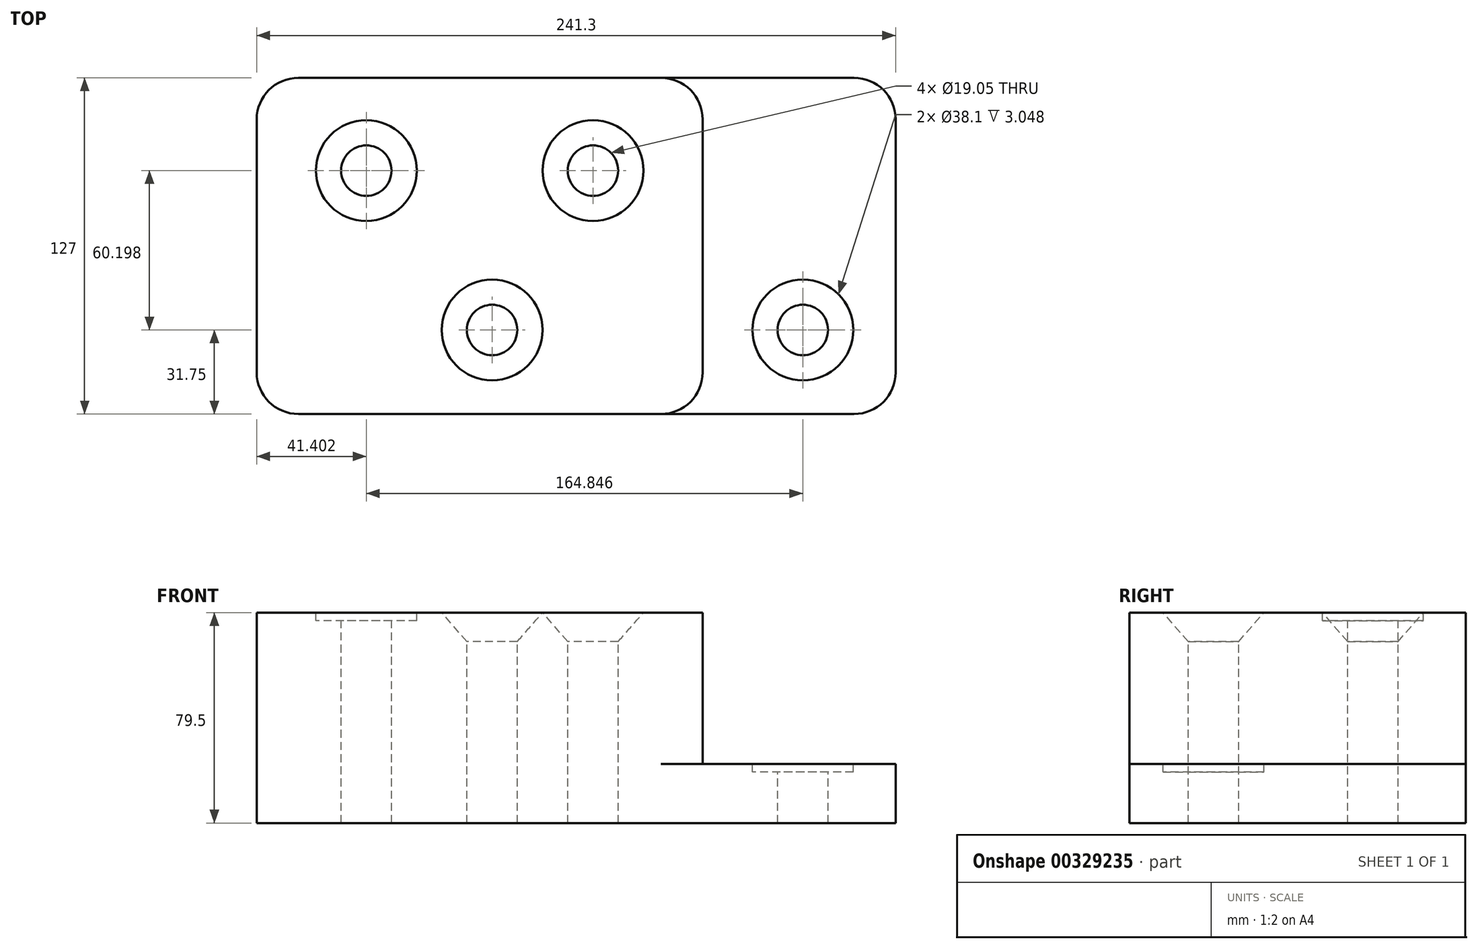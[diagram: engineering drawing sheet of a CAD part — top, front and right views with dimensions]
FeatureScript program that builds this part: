
annotation { "Feature Type Name" : "Feature", "Feature Type Description" : "" }
export const myFeature = defineFeature(function(context is Context, id is Id, definition is map)
    precondition{}
    {
        {
            var Q0;
            Q0=qCreatedBy(makeId("Front.planeOp"),FACE);
            var sketch = newSketch(context, id + "F0", { "sketchPlane" : qUnion([Q0])});
            skLineSegment(sketch, "E0", {"start": v(0, 0) * mm, "end": v(0, 79.5) * mm});
            skLineSegment(sketch, "E1", {"start": v(0, 79.5) * mm, "end": v(168.4, 79.5) * mm});
            skLineSegment(sketch, "E2", {"start": v(168.4, 79.5) * mm, "end": v(168.4, 22.35) * mm});
            skLineSegment(sketch, "E3", {"start": v(168.4, 22.35) * mm, "end": v(241.3, 22.35) * mm});
            skLineSegment(sketch, "E4", {"start": v(241.3, 22.35) * mm, "end": v(241.3, 0) * mm});
            skLineSegment(sketch, "E5", {"start": v(241.3, 0) * mm, "end": v(0, 0) * mm});
            skSolve(sketch);
        }
        {
            var Q0;
            Q0 = qSketchRegion(id + "F0", true);
            extrude(context, id + "F1", {"entities" : qUnion([Q0]), "depth" : 127 * mm});
        }
        {
            var Q0;
            Q0=makeQuery(id+"F1.opExtrude","CAP_EDGE",EDGE,{"disambiguationData":[OSD([sQuery(id+"F0.wireOp",EDGE,"E4")])],"isStart":false});
            var Q1;
            Q1=makeQuery(id+"F1.opExtrude","CAP_EDGE",EDGE,{"disambiguationData":[OSD([sQuery(id+"F0.wireOp",EDGE,"E4")])],"isStart":true});
            var Q2;
            Q2=makeQuery(id+"F1.opExtrude","CAP_EDGE",EDGE,{"disambiguationData":[OSD([sQuery(id+"F0.wireOp",EDGE,"E2")])],"isStart":true});
            var Q3;
            Q3=makeQuery(id+"F1.opExtrude","CAP_EDGE",EDGE,{"disambiguationData":[OSD([sQuery(id+"F0.wireOp",EDGE,"E2")])],"isStart":false});
            var Q4;
            Q4=makeQuery(id+"F1.opExtrude","CAP_EDGE",EDGE,{"disambiguationData":[OSD([sQuery(id+"F0.wireOp",EDGE,"E0")])],"isStart":false});
            var Q5;
            Q5=makeQuery(id+"F1.opExtrude","CAP_EDGE",EDGE,{"disambiguationData":[OSD([sQuery(id+"F0.wireOp",EDGE,"E0")])],"isStart":true});
            fillet(context, id + "F2", {"entities" : qUnion([Q0, Q1, Q2, Q3, Q4, Q5]), "radius" : 15.75 * mm, "tangentPropagation" : true, "allowEdgeOverflow" : false});
        }
        {
            var Q0;
            Q0=makeQuery(id+"F1.opExtrude","SWEPT_FACE",FACE,{"disambiguationData":[OSD([sQuery(id+"F0.wireOp",EDGE,"E1")])]});
            var sketch = newSketch(context, id + "F3", { "sketchPlane" : qUnion([Q0])});
            skPoint(sketch, "E6", {"position": v(88.9, -95.25) * mm});
            skPoint(sketch, "E7", {"position": v(127, -35.05) * mm});
            skPoint(sketch, "E8", {"position": v(41.4, -35.05) * mm});
            skPoint(sketch, "E9", {"position": v(206.25, -95.25) * mm});
            skSolve(sketch);
        }
        {
            var Q0;
            Q0=sQuery(id+"F3.wireOp",VERTEX,"E8");
            var Q1;
            Q1=sQuery(id+"F3.wireOp",VERTEX,"E9");
            var Q2;
            Q2=makeQuery(id+"F1.opExtrude","SWEPT_BODY",BODY,{"disambiguationData":[OSD([sQuery(id+"F0.wireOp",EDGE,"E0"),sQuery(id+"F0.wireOp",EDGE,"E1"),sQuery(id+"F0.wireOp",EDGE,"E2"),sQuery(id+"F0.wireOp",EDGE,"E3"),sQuery(id+"F0.wireOp",EDGE,"E4"),sQuery(id+"F0.wireOp",EDGE,"E5")])]});
            hole(context, id + "F4", {"style" : HoleStyle.C_BORE, "endStyle" : HoleEndStyle.THROUGH, "holeDiameter" : 19.05 * mm, "cBoreDiameter" : 38.1 * mm, "cBoreDepth" : 3.05 * mm, "tappedDepth" : 12.7 * mm, "tapClearance" : 3, "locations" : qUnion([Q0, Q1]), "scope" : qUnion([Q2])});
        }
        {
            var Q0;
            Q0=sQuery(id+"F3.wireOp",VERTEX,"E7");
            var Q1;
            Q1=sQuery(id+"F3.wireOp",VERTEX,"E6");
            var Q2;
            Q2=makeQuery(id+"F1.opExtrude","SWEPT_BODY",BODY,{"disambiguationData":[OSD([sQuery(id+"F0.wireOp",EDGE,"E0"),sQuery(id+"F0.wireOp",EDGE,"E1"),sQuery(id+"F0.wireOp",EDGE,"E2"),sQuery(id+"F0.wireOp",EDGE,"E3"),sQuery(id+"F0.wireOp",EDGE,"E4"),sQuery(id+"F0.wireOp",EDGE,"E5")])]});
            hole(context, id + "F5", {"style" : HoleStyle.C_SINK, "endStyle" : HoleEndStyle.THROUGH, "holeDiameter" : 19.05 * mm, "cSinkDiameter" : 38.1 * mm, "cSinkAngle" : 82 * degree, "tappedDepth" : 12.7 * mm, "tapClearance" : 3, "locations" : qUnion([Q0, Q1]), "scope" : qUnion([Q2])});
        }
    });
